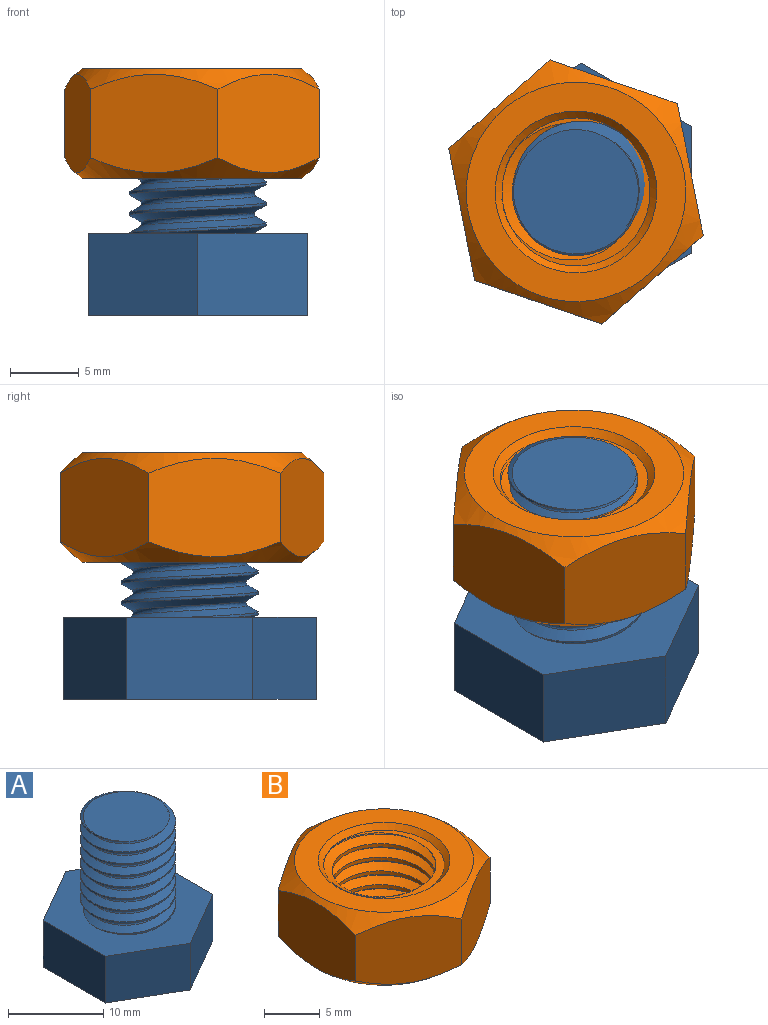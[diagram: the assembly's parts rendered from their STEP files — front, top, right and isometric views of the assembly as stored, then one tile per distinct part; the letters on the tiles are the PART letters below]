
ASSEMBLY  parts=2 mates=1
PART A: 20 faces, bbox 16.4x18.9x19 mm
  f0: plane 8x6mm, normal (-0.5,0.87,0), area 55.4mm2, adj f1,f5,f6,f7
  f1: plane 9.24x6mm, normal (-1,0,0), area 55.4mm2, adj f0,f2,f6,f7
  f2: plane 8x6mm, normal (-0.5,-0.87,0), area 55.4mm2, adj f1,f3,f6,f7
  f3: plane 8x6mm, normal (0.5,-0.87,0), area 55.4mm2, adj f2,f4,f6,f7
  f4: plane 9.24x6mm, normal (1,0,0), area 55.4mm2, adj f3,f5,f6,f7
  f5: plane 8x6mm, normal (0.5,0.87,0), area 55.4mm2, adj f0,f4,f6,f7
  f6: plane 18.89x16.42mm, normal (0,0,1), area 156.9mm2, adj f0,f1,f2,f3,f4,f5,f8,f10
  f7: plane 18.48x16mm, normal (0,0,-1), area 188.4mm2, adj f0,f1,f2,f3,f4,f5,f13,f14
  f8: cylinder r=5mm len=12mm, axis (0,0,-1), area 79.4mm2, adj f6,f9,f11,f12
  f9: plane 9.55x9.49mm, normal (0,0,1), area 64.8mm2, adj f8,f10,f11,f12
  f10: bspline ~13.13x9.67mm, area 87.2mm2, adj f6,f9,f11,f12
  f11: bspline ~13.22x11.55mm, area 216.5mm2, adj f6,f8,f9,f10
  f12: bspline ~12.97x11.55mm, area 217.1mm2, adj f6,f8,f9,f10
  f13: plane 4x3.1mm, normal (0.5,0.87,0), area 14.3mm2, adj f7,f14,f18,f19
  f14: plane 4x3.58mm, normal (1,0,0), area 14.3mm2, adj f7,f13,f15,f19
  f15: plane 4x3.1mm, normal (0.5,-0.87,0), area 14.3mm2, adj f7,f14,f16,f19
  f16: plane 4x3.1mm, normal (-0.5,-0.87,0), area 14.3mm2, adj f7,f15,f17,f19
  f17: plane 4x3.58mm, normal (-1,0,0), area 14.3mm2, adj f7,f16,f18,f19
  f18: plane 4x3.1mm, normal (-0.5,0.87,0), area 14.3mm2, adj f7,f13,f17,f19
  f19: plane 7.16x6.2mm, normal (0,0,-1), area 33.3mm2, adj f13,f14,f15,f16,f17,f18
PART B: 20 faces, bbox 20x20x8.6 mm
  f0: plane 16.02x16.02mm, normal (0,0,1), area 92.3mm2, adj f3,f13
  f1: plane 16.02x16.02mm, normal (0,0,-1), area 92.3mm2, adj f2,f12
  f2: cone r=5.9mm half-angle=45deg, axis (0,0,-1), area 25.1mm2, adj f1,f7,f9
  f3: cone r=5.4mm half-angle=45deg, axis (0,0,1), area 25.1mm2, adj f0,f8,f10
  f4: bspline ~12.61x10.92mm, area 139.2mm2, adj f6,f7,f8,f9,f10,f11
  f5: bspline ~12.61x10.92mm, area 139.1mm2, adj f6,f7,f8,f9,f10,f11
  f6: bspline ~12.77x11.06mm, area 35mm2, adj f4,f5,f7,f8
  f7: plane 5.47x1.88mm, normal (0,0,1), area 0.5mm2, adj f2,f4,f5,f6
  f8: plane 4.08x4mm, normal (0,0,-1), area 0.5mm2, adj f3,f4,f5,f6
  f9: plane 11.18x10.98mm, normal (0,0,-1), area 12.9mm2, adj f2,f4,f5,f11
  f10: plane 11.18x11.18mm, normal (0,0,1), area 12.9mm2, adj f3,f4,f5,f11
  f11: cylinder r=4.65mm len=9.3mm, axis (0,0,-1), area 51.1mm2, adj f4,f5,f9,f10
  f12: cone r=11.01mm half-angle=50.2deg, axis (0,0,1), area 63.3mm2, adj f1,f14,f15,f16,f17,f18,f19
  f13: cone r=11.01mm half-angle=50.2deg, axis (0,0,-1), area 63.3mm2, adj f0,f14,f15,f16,f17,f18,f19
  f14: plane 8.5x7.2mm, normal (0.5,0.87,0), area 63.1mm2, adj f12,f13,f15,f19
  f15: plane 9.82x7.19mm, normal (1,0,0), area 63.1mm2, adj f12,f13,f14,f16
  f16: plane 8.5x7.2mm, normal (0.5,-0.87,0), area 63.1mm2, adj f12,f13,f15,f17
  f17: plane 8.5x7.2mm, normal (-0.5,-0.87,0), area 63.1mm2, adj f12,f13,f16,f18
  f18: plane 9.82x7.19mm, normal (-1,0,0), area 63.1mm2, adj f12,f13,f17,f19
  f19: plane 8.5x7.2mm, normal (-0.5,0.87,0), area 63.1mm2, adj f12,f13,f14,f18
PLACE A t=(-54.99,-19.75,-7.42)mm fixed
PLACE B rot(axis=(0.81,0.58,0),180deg) t=(-30.41,-19.93,10.58)mm
MATE revolute B.f12 <-> A.f9  axis (0,0,1) through (-30.41,-19.93,10.58)mm
